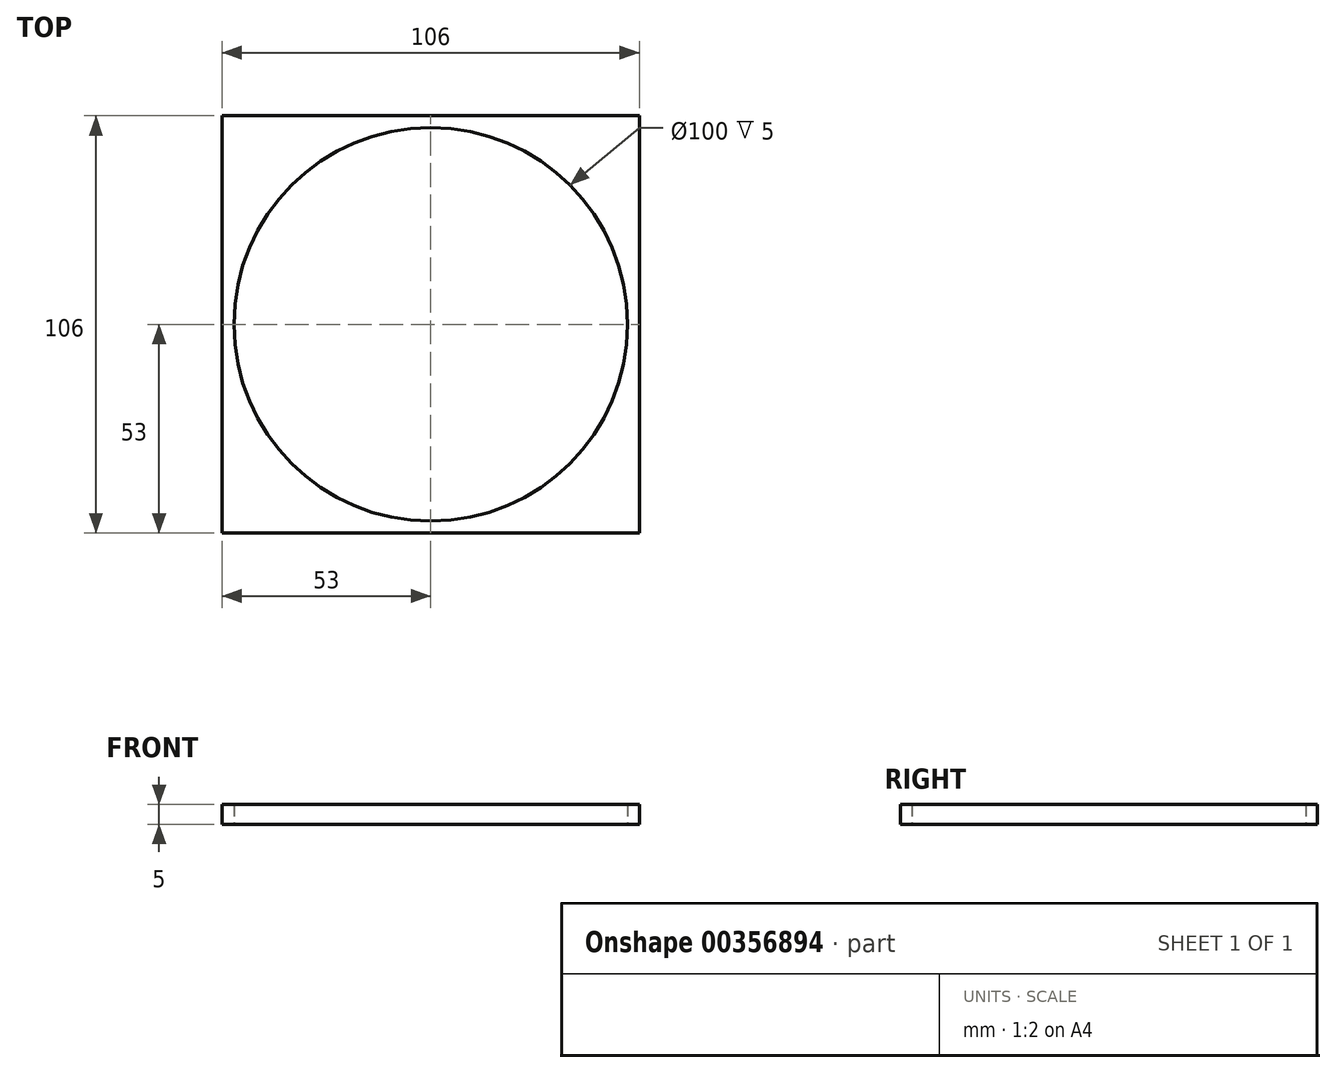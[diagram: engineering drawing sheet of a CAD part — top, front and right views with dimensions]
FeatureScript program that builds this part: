
annotation { "Feature Type Name" : "Feature", "Feature Type Description" : "" }
export const myFeature = defineFeature(function(context is Context, id is Id, definition is map)
    precondition{}
    {
        {
            var Q0;
            Q0=qCreatedBy(makeId("Top.planeOp"),FACE);
            var sketch = newSketch(context, id + "F0", { "sketchPlane" : qUnion([Q0])});
            skCircle(sketch, "E0", {"center": v(0, 0) * mm, "radius": 50 * mm});
            skLineSegment(sketch, "E1.bottom", {"start": v(53, 53) * mm, "end": v(-53, 53) * mm});
            skLineSegment(sketch, "E1.top", {"start": v(53, -53) * mm, "end": v(-53, -53) * mm});
            skLineSegment(sketch, "E1.left", {"start": v(53, 53) * mm, "end": v(53, -53) * mm});
            skLineSegment(sketch, "E1.right", {"start": v(-53, 53) * mm, "end": v(-53, -53) * mm});
            skSolve(sketch);
        }
        {
            var Q0;
            Q0=makeQuery(id+"F0.imprint","IMPRINT",FACE,{"disambiguationData":[TD([[makeQuery(id+"F0.imprint","IMPRINT",EDGE,{"derivedFrom":sQuery(id+"F0.wireOp",EDGE,"E0")}),-1.0]])]});
            extrude(context, id + "F1", {"entities" : qUnion([Q0]), "depth" : 5 * mm, "offsetDistance" : 25 * mm});
        }
    });
